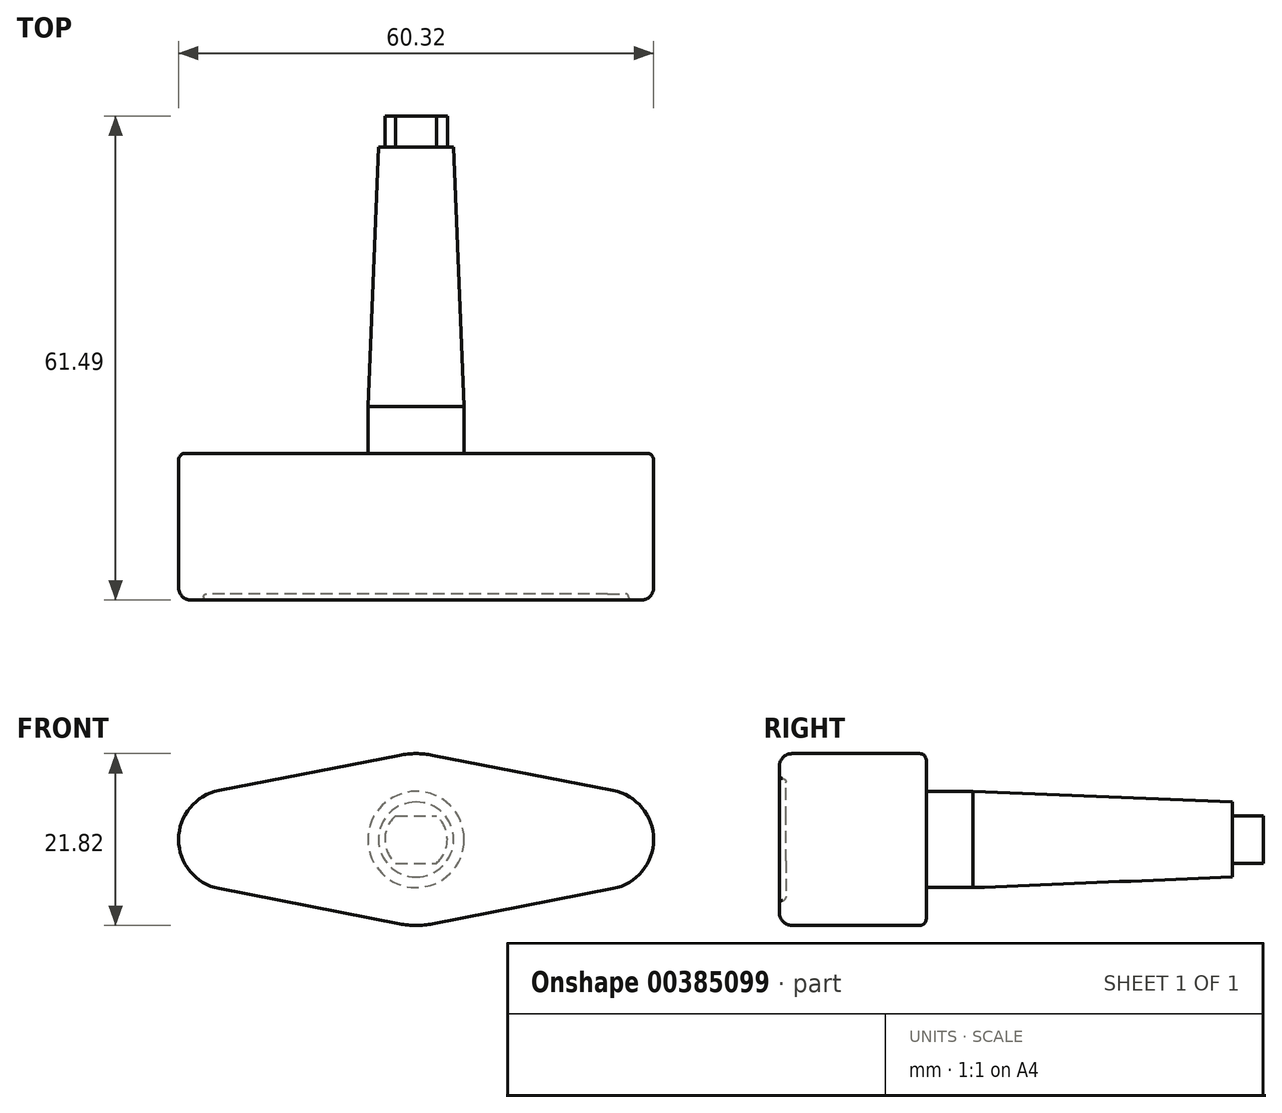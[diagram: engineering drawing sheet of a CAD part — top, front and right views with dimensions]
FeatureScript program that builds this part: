
annotation { "Feature Type Name" : "Feature", "Feature Type Description" : "" }
export const myFeature = defineFeature(function(context is Context, id is Id, definition is map)
    precondition{}
    {
        {
            var Q0;
            Q0=qCreatedBy(makeId("Front.planeOp"),FACE);
            var sketch = newSketch(context, id + "F0", { "sketchPlane" : qUnion([Q0])});
            skArc(sketch, "E0", {"start": v(-25.03, 6.23) * mm, "mid": v(-28.71, 4.04) * mm, "end": v(-30.16, 0) * mm});
            skLineSegment(sketch, "E1", {"start": v(-2.09, 10.7) * mm, "end": v(-25.03, 6.23) * mm});
            skLineSegment(sketch, "E2.MirrorCS", {"start": v(2.09, 10.7) * mm, "end": v(25.03, 6.23) * mm});
            skArc(sketch, "E3.MirrorCS", {"start": v(25.03, 6.23) * mm, "mid": v(28.71, 4.04) * mm, "end": v(30.16, 0) * mm});
            skArc(sketch, "E4.MirrorCS", {"start": v(-25.03, -6.23) * mm, "mid": v(-28.71, -4.04) * mm, "end": v(-30.16, 0) * mm});
            skArc(sketch, "E5.MirrorCS", {"start": v(25.03, -6.23) * mm, "mid": v(28.71, -4.04) * mm, "end": v(30.16, 0) * mm});
            skLineSegment(sketch, "E6.MirrorCS", {"start": v(2.09, -10.7) * mm, "end": v(25.03, -6.23) * mm});
            skLineSegment(sketch, "E7.MirrorCS", {"start": v(-2.09, -10.7) * mm, "end": v(-25.03, -6.23) * mm});
            skArc(sketch, "E8", {"start": v(2.09, 10.7) * mm, "mid": v(0, 10.9) * mm, "end": v(-2.09, 10.7) * mm});
            skArc(sketch, "E9.trimOffspring", {"start": v(-2.09, -10.7) * mm, "mid": v(0, -10.9) * mm, "end": v(2.09, -10.7) * mm});
            skCircle(sketch, "E10", {"center": v(0, 0) * mm, "radius": 6.1 * mm});
            skSolve(sketch);
        }
        {
            var Q0;
            Q0=makeQuery(id+"F0.imprint","IMPRINT",FACE,{"disambiguationData":[TD([[makeQuery(id+"F0.imprint","IMPRINT",EDGE,{"derivedFrom":sQuery(id+"F0.wireOp",EDGE,"E0")}),1.0]])]});
            var Q1;
            Q1=makeQuery(id+"F0.imprint","IMPRINT",FACE,{"disambiguationData":[TD([[makeQuery(id+"F0.imprint","IMPRINT",EDGE,{"derivedFrom":sQuery(id+"F0.wireOp",EDGE,"E10")}),1.0]])]});
            extrude(context, id + "F1", {"entities" : qUnion([Q0, Q1]), "depth" : 18.64 * mm});
        }
        {
            var Q0;
            Q0=makeQuery(id+"F1.opExtrude","CAP_FACE",FACE,{"disambiguationData":[OSD([sQuery(id+"F0.wireOp",EDGE,"E0"),sQuery(id+"F0.wireOp",EDGE,"E1"),sQuery(id+"F0.wireOp",EDGE,"E2.MirrorCS"),sQuery(id+"F0.wireOp",EDGE,"E3.MirrorCS"),sQuery(id+"F0.wireOp",EDGE,"E4.MirrorCS"),sQuery(id+"F0.wireOp",EDGE,"E5.MirrorCS"),sQuery(id+"F0.wireOp",EDGE,"E6.MirrorCS"),sQuery(id+"F0.wireOp",EDGE,"E7.MirrorCS"),sQuery(id+"F0.wireOp",EDGE,"E8"),sQuery(id+"F0.wireOp",EDGE,"E9.trimOffspring")])],"isStart":false});
            fillet(context, id + "F2", {"entities" : qUnion([Q0]), "radius" : 1.57 * mm, "tangentPropagation" : true, "allowEdgeOverflow" : false});
        }
        {
            var Q0;
            Q0=makeQuery(id+"F1.opExtrude","CAP_FACE",FACE,{"disambiguationData":[OSD([sQuery(id+"F0.wireOp",EDGE,"E0"),sQuery(id+"F0.wireOp",EDGE,"E1"),sQuery(id+"F0.wireOp",EDGE,"E2.MirrorCS"),sQuery(id+"F0.wireOp",EDGE,"E3.MirrorCS"),sQuery(id+"F0.wireOp",EDGE,"E4.MirrorCS"),sQuery(id+"F0.wireOp",EDGE,"E5.MirrorCS"),sQuery(id+"F0.wireOp",EDGE,"E6.MirrorCS"),sQuery(id+"F0.wireOp",EDGE,"E7.MirrorCS"),sQuery(id+"F0.wireOp",EDGE,"E8"),sQuery(id+"F0.wireOp",EDGE,"E9.trimOffspring")])],"isStart":false});
            var sketch = newSketch(context, id + "F3", { "sketchPlane" : qUnion([Q0])});
            skLineSegment(sketch, "E11.0.0", {"start": v(-1.79, 9.16) * mm, "end": v(-24.73, 4.69) * mm});
            skArc(sketch, "E11.0.1", {"start": v(-24.73, 4.69) * mm, "mid": v(-28.59, 0) * mm, "end": v(-24.73, -4.69) * mm});
            skLineSegment(sketch, "E11.0.2", {"start": v(-24.73, -4.69) * mm, "end": v(-1.79, -9.16) * mm});
            skArc(sketch, "E11.0.3", {"start": v(-1.79, -9.16) * mm, "mid": v(0, -9.33) * mm, "end": v(1.79, -9.16) * mm});
            skLineSegment(sketch, "E11.0.4", {"start": v(1.79, -9.16) * mm, "end": v(24.73, -4.69) * mm});
            skArc(sketch, "E11.0.5", {"start": v(24.73, -4.69) * mm, "mid": v(28.59, 0) * mm, "end": v(24.73, 4.69) * mm});
            skLineSegment(sketch, "E11.0.6", {"start": v(24.73, 4.69) * mm, "end": v(1.79, 9.16) * mm});
            skArc(sketch, "E11.0.7", {"start": v(1.79, 9.16) * mm, "mid": v(0, 9.33) * mm, "end": v(-1.79, 9.16) * mm});
            skArc(sketch, "E12.0", {"start": v(1.48, 7.6) * mm, "mid": v(0, 7.74) * mm, "end": v(-1.48, 7.6) * mm});
            skLineSegment(sketch, "E12.1", {"start": v(24.42, 3.13) * mm, "end": v(1.48, 7.6) * mm});
            skLineSegment(sketch, "E12.2", {"start": v(-1.48, 7.6) * mm, "end": v(-24.42, 3.13) * mm});
            skArc(sketch, "E12.3", {"start": v(24.42, -3.13) * mm, "mid": v(27, 0) * mm, "end": v(24.42, 3.13) * mm});
            skArc(sketch, "E12.4", {"start": v(-24.42, 3.13) * mm, "mid": v(-27, 0) * mm, "end": v(-24.42, -3.13) * mm});
            skLineSegment(sketch, "E12.5", {"start": v(-24.42, -3.13) * mm, "end": v(-1.48, -7.6) * mm});
            skArc(sketch, "E12.6", {"start": v(-1.48, -7.6) * mm, "mid": v(0, -7.74) * mm, "end": v(1.48, -7.6) * mm});
            skLineSegment(sketch, "E12.7", {"start": v(1.48, -7.6) * mm, "end": v(24.42, -3.13) * mm});
            skSolve(sketch);
        }
        {
            var Q0;
            Q0=makeQuery(id+"F3.imprint","IMPRINT",FACE,{"disambiguationData":[TD([[makeQuery(id+"F3.imprint","IMPRINT",EDGE,{"derivedFrom":sQuery(id+"F3.wireOp",EDGE,"E12.0")}),1.0]])]});
            extrude(context, id + "F4", {"entities" : qUnion([Q0]), "operationType" : NewBodyOperationType.REMOVE, "oppositeDirection" : true, "depth" : 0.81 * mm});
        }
        {
            var Q0;
            Q0=makeQuery(id+"F4.boolean.opBoolean","COPY",FACE,{"derivedFrom":makeQuery(id+"F4.opExtrude","CAP_FACE",FACE,{"disambiguationData":[OSD([sQuery(id+"F3.wireOp",EDGE,"E12.0"),sQuery(id+"F3.wireOp",EDGE,"E12.1"),sQuery(id+"F3.wireOp",EDGE,"E12.2"),sQuery(id+"F3.wireOp",EDGE,"E12.3"),sQuery(id+"F3.wireOp",EDGE,"E12.4"),sQuery(id+"F3.wireOp",EDGE,"E12.5"),sQuery(id+"F3.wireOp",EDGE,"E12.6"),sQuery(id+"F3.wireOp",EDGE,"E12.7")])],"isStart":false})});
            fillet(context, id + "F5", {"entities" : qUnion([Q0]), "radius" : 0.4 * mm, "tangentPropagation" : true, "allowEdgeOverflow" : false});
        }
        {
            var Q0;
            Q0=makeQuery(id+"F4.boolean.opBoolean","COPY",FACE,{"derivedFrom":makeQuery(id+"F4.opExtrude","SWEPT_FACE",FACE,{"disambiguationData":[OSD([sQuery(id+"F3.wireOp",EDGE,"E12.2")])]})});
            fillet(context, id + "F6", {"entities" : qUnion([Q0]), "radius" : 0.4 * mm, "tangentPropagation" : true, "allowEdgeOverflow" : false});
        }
        {
            var Q0;
            Q0=makeQuery(id+"F1.opExtrude","CAP_FACE",FACE,{"disambiguationData":[OSD([sQuery(id+"F0.wireOp",EDGE,"E0"),sQuery(id+"F0.wireOp",EDGE,"E1"),sQuery(id+"F0.wireOp",EDGE,"E2.MirrorCS"),sQuery(id+"F0.wireOp",EDGE,"E3.MirrorCS"),sQuery(id+"F0.wireOp",EDGE,"E4.MirrorCS"),sQuery(id+"F0.wireOp",EDGE,"E5.MirrorCS"),sQuery(id+"F0.wireOp",EDGE,"E6.MirrorCS"),sQuery(id+"F0.wireOp",EDGE,"E7.MirrorCS"),sQuery(id+"F0.wireOp",EDGE,"E8"),sQuery(id+"F0.wireOp",EDGE,"E9.trimOffspring")])],"isStart":true});
            fillet(context, id + "F7", {"entities" : qUnion([Q0]), "radius" : 0.81 * mm, "tangentPropagation" : true, "allowEdgeOverflow" : false});
        }
        {
            var Q0;
            Q0=makeQuery(id+"F0.imprint","IMPRINT",FACE,{"disambiguationData":[TD([[makeQuery(id+"F0.imprint","IMPRINT",EDGE,{"derivedFrom":sQuery(id+"F0.wireOp",EDGE,"E10")}),1.0]])]});
            extrude(context, id + "F8", {"entities" : qUnion([Q0]), "operationType" : NewBodyOperationType.ADD, "oppositeDirection" : true, "depth" : 5.94 * mm});
        }
        {
            var Q0;
            Q0=makeQuery(id+"F8.opExtrude","CAP_FACE",FACE,{"disambiguationData":[OSD([sQuery(id+"F0.wireOp",EDGE,"E10")])],"isStart":false});
            cPlane(context, id + "F9", {"entities" : qUnion([Q0]), "cplaneType" : CPlaneType.OFFSET, "offset" : 32.94 * mm, "width" : 152.4 * mm, "height" : 152.4 * mm});
        }
        {
            var Q0;
            Q0=qCreatedBy(id+"F9.planeOp",FACE);
            var sketch = newSketch(context, id + "F10", { "sketchPlane" : qUnion([Q0])});
            skCircle(sketch, "E13", {"center": v(0, 0) * mm, "radius": 4.76 * mm});
            skSolve(sketch);
        }
        {
            var Q1;
            Q1=makeQuery(id+"F8.opExtrude","CAP_FACE",FACE,{"disambiguationData":[OSD([sQuery(id+"F0.wireOp",EDGE,"E10")])],"isStart":false});
            var Q2;
            Q2=makeQuery(id+"F10.imprint","IMPRINT",FACE,{"disambiguationData":[TD([[makeQuery(id+"F10.imprint","IMPRINT",EDGE,{"derivedFrom":sQuery(id+"F10.wireOp",EDGE,"E13")}),1.0]])]});
            loft(context, id + "F11", {"operationType" : NewBodyOperationType.ADD, "sheetProfilesArray" : [{ "sheetProfileEntities" : qUnion([Q1]) }, { "sheetProfileEntities" : qUnion([Q2]) }]});
        }
        {
            var Q0;
            Q0=makeQuery(id+"F11.opLoft","CAP_FACE",FACE,{"disambiguationData":[OSD([makeQuery(id+"F10.imprint","IMPRINT",FACE,{"disambiguationData":[TD([[makeQuery(id+"F10.imprint","IMPRINT",EDGE,{"derivedFrom":sQuery(id+"F10.wireOp",EDGE,"E13")}),1.0]])]})])],"isStart":true});
            var sketch = newSketch(context, id + "F12", { "sketchPlane" : qUnion([Q0])});
            skArc(sketch, "E14", {"start": v(-2.58, 3.02) * mm, "mid": v(-3.97, 0) * mm, "end": v(-2.58, -3.02) * mm});
            skLineSegment(sketch, "E15", {"start": v(0, 3.02) * mm, "end": v(2.58, 3.02) * mm});
            skLineSegment(sketch, "E16", {"start": v(0, 3.02) * mm, "end": v(-2.58, 3.02) * mm});
            skLineSegment(sketch, "E17", {"start": v(0, -3.02) * mm, "end": v(2.58, -3.02) * mm});
            skLineSegment(sketch, "E18", {"start": v(0, -3.02) * mm, "end": v(-2.58, -3.02) * mm});
            skArc(sketch, "E19.trimOffspring", {"start": v(2.58, -3.02) * mm, "mid": v(3.97, 0) * mm, "end": v(2.58, 3.02) * mm});
            skSolve(sketch);
        }
        {
            var Q0;
            Q0=makeQuery(id+"F12.imprint","IMPRINT",FACE,{"disambiguationData":[TD([[makeQuery(id+"F12.imprint","IMPRINT",EDGE,{"derivedFrom":sQuery(id+"F12.wireOp",EDGE,"E14")}),1.0]])]});
            extrude(context, id + "F13", {"entities" : qUnion([Q0]), "operationType" : NewBodyOperationType.ADD, "depth" : 3.96 * mm});
        }
    });
